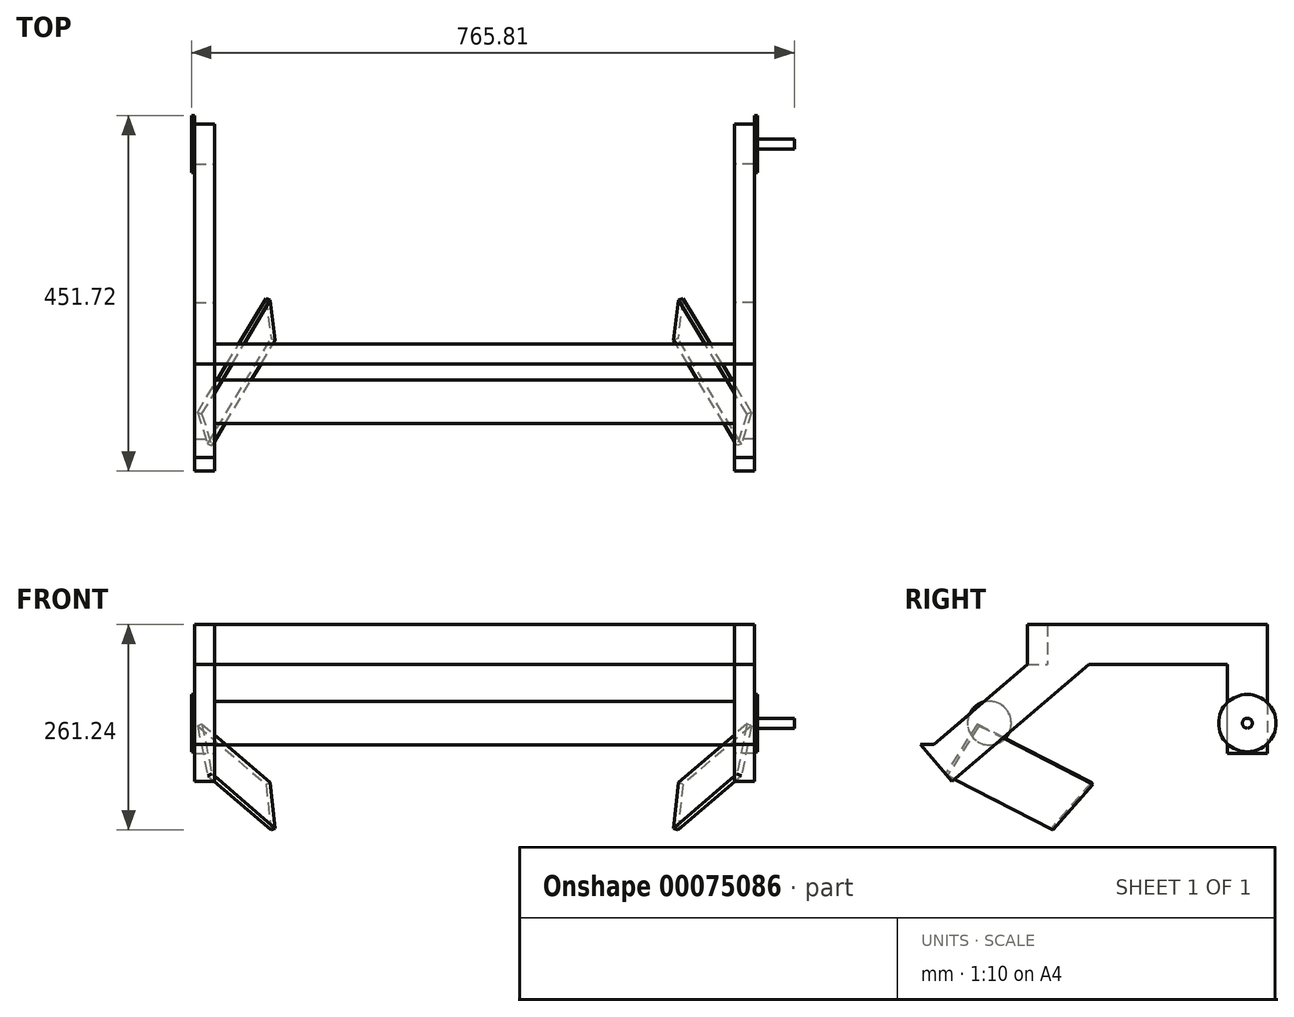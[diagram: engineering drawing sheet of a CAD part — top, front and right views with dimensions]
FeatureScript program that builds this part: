
annotation { "Feature Type Name" : "Feature", "Feature Type Description" : "" }
export const myFeature = defineFeature(function(context is Context, id is Id, definition is map)
    precondition{}
    {
        {
            var Q0;
            Q0=qCreatedBy(makeId("Right.planeOp"),FACE);
            var sketch = newSketch(context, id + "F0", { "sketchPlane" : qUnion([Q0])});
            skLineSegment(sketch, "E0", {"start": v(-94.16, 0) * mm, "end": v(-94.16, 112.68) * mm});
            skLineSegment(sketch, "E1", {"start": v(-94.16, 0) * mm, "end": v(-694.96, 0) * mm, "construction": true});
            skLineSegment(sketch, "E2", {"start": v(-476.75, 2.77) * mm, "end": v(-443.75, -35.84) * mm});
            skLineSegment(sketch, "E3", {"start": v(-443.75, -35.84) * mm, "end": v(-269.97, 112.68) * mm});
            skLineSegment(sketch, "E4", {"start": v(-94.16, 0) * mm, "end": v(-43.36, 0) * mm});
            skLineSegment(sketch, "E5", {"start": v(-476.75, 2.77) * mm, "end": v(-348.16, 112.68) * mm});
            skLineSegment(sketch, "E6", {"start": v(-348.16, 112.68) * mm, "end": v(-94.16, 112.68) * mm});
            skLineSegment(sketch, "E7", {"start": v(-68.76, 163.48) * mm, "end": v(-68.76, 112.68) * mm});
            skLineSegment(sketch, "E8", {"start": v(-68.76, 112.68) * mm, "end": v(-94.16, 112.68) * mm});
            skLineSegment(sketch, "E9", {"start": v(-68.76, 163.48) * mm, "end": v(-43.36, 163.48) * mm});
            skLineSegment(sketch, "E10", {"start": v(-348.16, 163.48) * mm, "end": v(-348.16, 112.68) * mm});
            skLineSegment(sketch, "E11", {"start": v(-348.16, 163.48) * mm, "end": v(-68.76, 163.48) * mm});
            skLineSegment(sketch, "E12", {"start": v(-43.36, 163.48) * mm, "end": v(-43.36, 0) * mm});
            skLineSegment(sketch, "E13", {"start": v(-476.75, 2.77) * mm, "end": v(-484.1, 11.38) * mm});
            skLineSegment(sketch, "E14", {"start": v(-484.1, 11.38) * mm, "end": v(-466.69, 11.38) * mm});
            skSolve(sketch);
        }
        {
            var Q0;
            Q0=qSketchRegion(id+"F0",true);
            extrude(context, id + "F1", {"entities" : qUnion([Q0]), "depth" : 25.4 * mm});
        }
        {
            var Q0;
            Q0=makeQuery(id+"F1.opExtrude","CAP_FACE",FACE,{"disambiguationData":[OSD([sQuery(id+"F0.wireOp",EDGE,"E0"),sQuery(id+"F0.wireOp",EDGE,"FzFAvqxY-UHcR-LB1o-9BGg-ITqtltGkoCg7"),sQuery(id+"F0.wireOp",EDGE,"9EqjKHUN-b0a3-5l8C-lEbD-YhtaKGnvM4r8"),sQuery(id+"F0.wireOp",EDGE,"O03rAtuE-vBr0-TGGL-qlow-hzOp0SjMRf3J"),sQuery(id+"F0.wireOp",EDGE,"EjQ2AoOY-oglP-w6Ik-A1Gc-PS80yBvVY6DT"),sQuery(id+"F0.wireOp",EDGE,"My8O57xa-rGE3-r1xm-LMVX-D7q3z3uxBNhY"),sQuery(id+"F0.wireOp",EDGE,"NvZxACeX-bEyG-zTEK-baQ0-WmrqGVVfxpHT"),sQuery(id+"F0.wireOp",EDGE,"Gs7LIxsz-L5wS-YETb-tkpd-3293kP4owoCf"),sQuery(id+"F0.wireOp",EDGE,"AIuwvOd5-8N9c-JBEI-UZta-CtQydD628jPl"),sQuery(id+"F0.wireOp",EDGE,"quivdLkZ-Yprh-0Sfe-2aDW-KqEX2wnIxKLM"),sQuery(id+"F0.wireOp",EDGE,"vIYmLUtE-QRm2-21qQ-54xk-VfLQgNpEU5oN")])],"isStart":true});
            cPlane(context, id + "F2", {"entities" : qUnion([Q0]), "cplaneType" : CPlaneType.OFFSET, "offset" : 330.2 * mm, "width" : 152.4 * mm, "height" : 152.4 * mm});
        }
        {
            var Q0;
            Q0=makeQuery(id+"F1.opExtrude","SWEPT_BODY",BODY,{"disambiguationData":[OSD([sQuery(id+"F0.wireOp",EDGE,"E0"),sQuery(id+"F0.wireOp",EDGE,"FzFAvqxY-UHcR-LB1o-9BGg-ITqtltGkoCg7"),sQuery(id+"F0.wireOp",EDGE,"9EqjKHUN-b0a3-5l8C-lEbD-YhtaKGnvM4r8"),sQuery(id+"F0.wireOp",EDGE,"O03rAtuE-vBr0-TGGL-qlow-hzOp0SjMRf3J"),sQuery(id+"F0.wireOp",EDGE,"EjQ2AoOY-oglP-w6Ik-A1Gc-PS80yBvVY6DT"),sQuery(id+"F0.wireOp",EDGE,"My8O57xa-rGE3-r1xm-LMVX-D7q3z3uxBNhY"),sQuery(id+"F0.wireOp",EDGE,"NvZxACeX-bEyG-zTEK-baQ0-WmrqGVVfxpHT"),sQuery(id+"F0.wireOp",EDGE,"Gs7LIxsz-L5wS-YETb-tkpd-3293kP4owoCf"),sQuery(id+"F0.wireOp",EDGE,"AIuwvOd5-8N9c-JBEI-UZta-CtQydD628jPl"),sQuery(id+"F0.wireOp",EDGE,"quivdLkZ-Yprh-0Sfe-2aDW-KqEX2wnIxKLM"),sQuery(id+"F0.wireOp",EDGE,"vIYmLUtE-QRm2-21qQ-54xk-VfLQgNpEU5oN")])]});
            var Q1;
            Q1=qCreatedBy(id+"F2.planeOp",FACE);
            mirror(context, id + "F3", {"entities" : qUnion([Q0]), "mirrorPlane" : qUnion([Q1])});
        }
        {
            var Q0;
            Q0=qCreatedBy(makeId("Right.planeOp"),FACE);
            var sketch = newSketch(context, id + "F4", { "sketchPlane" : qUnion([Q0])});
            skLineSegment(sketch, "E15.top", {"start": v(-443.75, -35.84) * mm, "end": v(-265.95, -35.84) * mm});
            skLineSegment(sketch, "E15.left", {"start": v(-443.76, 40.35) * mm, "end": v(-443.75, -35.84) * mm});
            skPoint(sketch, "E16", {"position": v(-94.16, 0) * mm});
            skLineSegment(sketch, "E17", {"start": v(-443.76, 40.35) * mm, "end": v(-259.13, 40.35) * mm});
            skLineSegment(sketch, "E18", {"start": v(-259.13, 40.35) * mm, "end": v(-272.57, -35.84) * mm});
            skSolve(sketch);
        }
        {
            var Q0;
            Q0=qSketchRegion(id+"F4",true);
            extrude(context, id + "F5", {"entities" : qUnion([Q0]), "depth" : 6.35 * mm, "hasSecondDirection" : true, "secondDirectionOppositeDirection" : true, "secondDirectionDepth" : 0.03 * mm});
        }
        {
            var Q0;
            Q0=makeQuery(id+"F5.opExtrude","SWEPT_BODY",BODY,{"disambiguationData":[OSD([sQuery(id+"F4.wireOp",EDGE,"E15.bottom"),sQuery(id+"F4.wireOp",EDGE,"E15.top"),sQuery(id+"F4.wireOp",EDGE,"E15.left"),sQuery(id+"F4.wireOp",EDGE,"E15.right")])]});
            var Q1;
            Q1=makeQuery(id+"F5.opExtrude","SWEPT_EDGE",EDGE,{"disambiguationData":[OSD([sQuery(id+"F4.wireOp",EDGE,"E15.top"),sQuery(id+"F4.wireOp",EDGE,"E15.left")])]});
            transform(context, id + "F6", {"entities" : qUnion([Q0]), "transformType" : TransformType.ROTATION, "transformAxis" : qUnion([Q1]), "angle" : 30 * degree, "makeCopy" : false});
        }
        {
            var Q0;
            Q0=makeQuery(id+"F5.opExtrude","SWEPT_BODY",BODY,{"disambiguationData":[OSD([sQuery(id+"F4.wireOp",EDGE,"E15.bottom"),sQuery(id+"F4.wireOp",EDGE,"E15.top"),sQuery(id+"F4.wireOp",EDGE,"E15.left"),sQuery(id+"F4.wireOp",EDGE,"E15.right")])]});
            var Q1;
            Q1=makeQuery(id+"F1.opExtrude","CAP_EDGE",EDGE,{"disambiguationData":[OSD([sQuery(id+"F0.wireOp",EDGE,"E3")])],"isStart":false});
            var Q2;
            Q2=makeQuery(id+"F1.opExtrude","CAP_EDGE",EDGE,{"disambiguationData":[OSD([sQuery(id+"F0.wireOp",EDGE,"E3")])],"isStart":false});
            transform(context, id + "F7", {"entities" : qUnion([Q0]), "transformType" : TransformType.ROTATION, "transformAxis" : qUnion([Q2]), "angle" : 30 * degree, "makeCopy" : false});
        }
        {
            var Q0;
            Q0=makeQuery(id+"F5.opExtrude","SWEPT_BODY",BODY,{"disambiguationData":[OSD([sQuery(id+"F4.wireOp",EDGE,"E15.bottom"),sQuery(id+"F4.wireOp",EDGE,"E15.top"),sQuery(id+"F4.wireOp",EDGE,"E15.left"),sQuery(id+"F4.wireOp",EDGE,"E15.right")])]});
            var Q1;
            Q1=qCreatedBy(id+"F2.planeOp",FACE);
            mirror(context, id + "F8", {"entities" : qUnion([Q0]), "mirrorPlane" : qUnion([Q1])});
        }
        {
            var Q0;
            Q0=makeQuery(id+"F1.opExtrude","CAP_FACE",FACE,{"disambiguationData":[OSD([sQuery(id+"F0.wireOp",EDGE,"E0"),sQuery(id+"F0.wireOp",EDGE,"E2"),sQuery(id+"F0.wireOp",EDGE,"pgoFbepU-owTZ-p2G4-Cijl-EE9JvyGf2Y0f"),sQuery(id+"F0.wireOp",EDGE,"E3"),sQuery(id+"F0.wireOp",EDGE,"E4"),sQuery(id+"F0.wireOp",EDGE,"iuQHUlL3-SlOq-g9oo-7UXj-QUPuSQ9YM9Pp"),sQuery(id+"F0.wireOp",EDGE,"x3V7TLua-p2kA-iWFB-Oiq2-3fw1J4Rm9Nzl"),sQuery(id+"F0.wireOp",EDGE,"HaroZBpW-mr0K-WHzW-76yz-0Yw9BgI9cujc"),sQuery(id+"F0.wireOp",EDGE,"E5"),sQuery(id+"F0.wireOp",EDGE,"d2bHa0wy-btQe-sPfS-NveK-YwPCg79GWIoV"),sQuery(id+"F0.wireOp",EDGE,"E6"),sQuery(id+"F0.wireOp",EDGE,"U9c3RjT5-WkM9-Yazo-CPmD-timwblRfDxUe"),sQuery(id+"F0.wireOp",EDGE,"E9")])],"isStart":false});
            var sketch = newSketch(context, id + "F9", { "sketchPlane" : qUnion([Q0])});
            skCircle(sketch, "E19", {"center": v(-68.76, 38.1) * mm, "radius": 36.38 * mm});
            skLineSegment(sketch, "E20", {"start": v(-68.76, 38.1) * mm, "end": v(-533.27, 38.1) * mm, "construction": true});
            skSolve(sketch);
        }
        {
            var Q0;
            Q0=qCreatedBy(id+"F2.planeOp",FACE);
            var sketch = newSketch(context, id + "F10", { "sketchPlane" : qUnion([Q0])});
            skLineSegment(sketch, "E21", {"start": v(443.75, -35.84) * mm, "end": v(444.2, -35.24) * mm});
            skLineSegment(sketch, "E22.bottom", {"start": v(348.16, 163.48) * mm, "end": v(322.76, 163.48) * mm});
            skLineSegment(sketch, "E22.top", {"start": v(348.16, 112.67) * mm, "end": v(322.76, 112.67) * mm});
            skLineSegment(sketch, "E22.left", {"start": v(348.16, 163.48) * mm, "end": v(348.16, 112.67) * mm});
            skLineSegment(sketch, "E22.right", {"start": v(322.76, 163.48) * mm, "end": v(322.76, 112.67) * mm});
            skCircle(sketch, "E23", {"center": v(396.32, 38.1) * mm, "radius": 27.76 * mm});
            skLineSegment(sketch, "E24", {"start": v(440.9, 0) * mm, "end": v(-33.44, 0) * mm, "construction": true});
            skSolve(sketch);
        }
        {
            var Q0;
            Q0=qSketchRegion(id+"F10",true);
            extrude(context, id + "F11", {"entities" : qUnion([Q0]), "depth" : 330.2 * mm, "hasSecondDirection" : true, "secondDirectionOppositeDirection" : true, "secondDirectionDepth" : 330.2 * mm});
        }
        {
            var Q0;
            Q0=makeQuery(id+"F1.opExtrude","CAP_FACE",FACE,{"disambiguationData":[OSD([sQuery(id+"F0.wireOp",EDGE,"E0"),sQuery(id+"F0.wireOp",EDGE,"FzFAvqxY-UHcR-LB1o-9BGg-ITqtltGkoCg7"),sQuery(id+"F0.wireOp",EDGE,"AIuwvOd5-8N9c-JBEI-UZta-CtQydD628jPl"),sQuery(id+"F0.wireOp",EDGE,"quivdLkZ-Yprh-0Sfe-2aDW-KqEX2wnIxKLM"),sQuery(id+"F0.wireOp",EDGE,"E2"),sQuery(id+"F0.wireOp",EDGE,"fvPKbQlq-eRBd-6paL-miDW-omm5LcvnkUsL"),sQuery(id+"F0.wireOp",EDGE,"pgoFbepU-owTZ-p2G4-Cijl-EE9JvyGf2Y0f"),sQuery(id+"F0.wireOp",EDGE,"E3"),sQuery(id+"F0.wireOp",EDGE,"E4"),sQuery(id+"F0.wireOp",EDGE,"ksixRlnq-MVLY-tKXa-FHLY-OIVs7AOosSiE")])],"isStart":false});
            var sketch = newSketch(context, id + "F12", { "sketchPlane" : qUnion([Q0])});
            skCircle(sketch, "E25", {"center": v(-68.76, 38.1) * mm, "radius": 6.35 * mm});
            skCircle(sketch, "E26", {"center": v(-68.76, 38.1) * mm, "radius": 36.33 * mm});
            skSolve(sketch);
        }
        {
            var Q0;
            Q0=makeQuery(id+"F12.imprint","IMPRINT",FACE,{"disambiguationData":[TD([[makeQuery(id+"F12.imprint","IMPRINT",EDGE,{"derivedFrom":sQuery(id+"F12.wireOp",EDGE,"E25")}),1.0]])]});
            var Q1;
            Q1=sQuery(id+"F12.wireOp",EDGE,"E25");
            extrude(context, id + "F13", {"entities" : qUnion([Q0]), "operationType" : NewBodyOperationType.ADD, "surfaceEntities" : qUnion([Q1]), "depth" : 50.8 * mm});
        }
        {
            var Q0;
            Q0 = qSketchRegion(id + "F9", true);
            extrude(context, id + "F14", {"entities" : qUnion([Q0]), "depth" : 3.8 * mm});
        }
        {
            var Q0;
            Q0=makeQuery(id+"F14.opExtrude","SWEPT_BODY",BODY,{"disambiguationData":[OSD([sQuery(id+"F9.wireOp",EDGE,"E19")])]});
            var Q1;
            Q1=qCreatedBy(id+"F2.planeOp",FACE);
            mirror(context, id + "F15", {"entities" : qUnion([Q0]), "mirrorPlane" : qUnion([Q1])});
        }
    });
